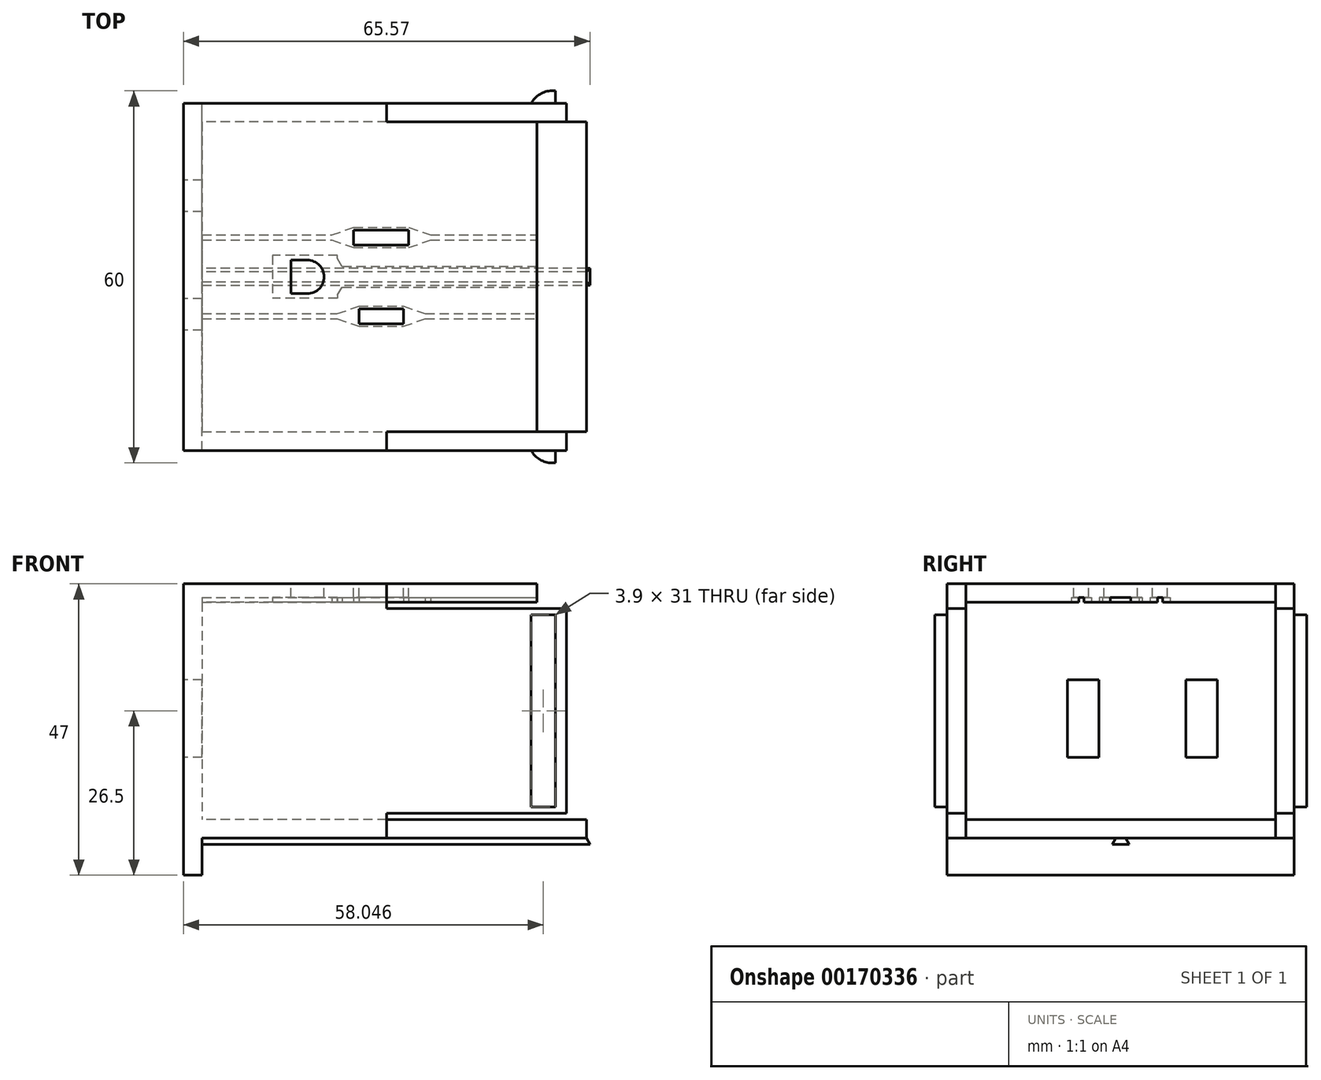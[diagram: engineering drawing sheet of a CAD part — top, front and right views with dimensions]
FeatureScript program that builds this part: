
annotation { "Feature Type Name" : "Feature", "Feature Type Description" : "" }
export const myFeature = defineFeature(function(context is Context, id is Id, definition is map)
    precondition{}
    {
        {
            var Q0;
            Q0=qCreatedBy(makeId("Top.planeOp"),FACE);
            var sketch = newSketch(context, id + "F0", { "sketchPlane" : qUnion([Q0])});
            skLineSegment(sketch, "E0", {"start": v(-33.77, 22.66) * mm, "end": v(-33.77, -33.34) * mm});
            skLineSegment(sketch, "E1", {"start": v(-33.77, -33.34) * mm, "end": v(31.23, -33.34) * mm});
            skLineSegment(sketch, "E2", {"start": v(31.23, -33.34) * mm, "end": v(31.23, 22.66) * mm});
            skLineSegment(sketch, "E3", {"start": v(31.23, 22.66) * mm, "end": v(-33.77, 22.66) * mm});
            skSolve(sketch);
        }
        {
            var Q0;
            Q0=makeQuery(id+"F0.imprint","IMPRINT",FACE,{"disambiguationData":[TD([[makeQuery(id+"F0.imprint","IMPRINT",EDGE,{"derivedFrom":sQuery(id+"F0.wireOp",EDGE,"E0")}),1.0]])]});
            extrude(context, id + "F1", {"entities" : qUnion([Q0]), "depth" : 41 * mm});
        }
        {
            var Q0;
            Q0=makeQuery(id+"F1.opExtrude","SWEPT_FACE",FACE,{"disambiguationData":[OSD([sQuery(id+"F0.wireOp",EDGE,"E2")])]});
            shell(context, id + "F2", {"entities" : qUnion([Q0]), "thickness" : 3 * mm});
        }
        {
            var Q0;
            Q0=makeQuery(id+"F1.opExtrude","SWEPT_FACE",FACE,{"disambiguationData":[OSD([sQuery(id+"F0.wireOp",EDGE,"E0")])]});
            var sketch = newSketch(context, id + "F3", { "sketchPlane" : qUnion([Q0])});
            skLineSegment(sketch, "E4.bottom", {"start": v(-10.28, 25.5) * mm, "end": v(-5.16, 25.5) * mm});
            skLineSegment(sketch, "E4.top", {"start": v(-10.28, 13) * mm, "end": v(-5.16, 13) * mm});
            skLineSegment(sketch, "E4.left", {"start": v(-10.28, 25.5) * mm, "end": v(-10.28, 13) * mm});
            skLineSegment(sketch, "E4.right", {"start": v(-5.16, 25.5) * mm, "end": v(-5.16, 13) * mm});
            skLineSegment(sketch, "E5.bottom", {"start": v(8.84, 25.5) * mm, "end": v(13.96, 25.5) * mm});
            skLineSegment(sketch, "E5.top", {"start": v(8.84, 13) * mm, "end": v(13.96, 13) * mm});
            skLineSegment(sketch, "E5.left", {"start": v(8.84, 25.5) * mm, "end": v(8.84, 13) * mm});
            skLineSegment(sketch, "E5.right", {"start": v(13.96, 25.5) * mm, "end": v(13.96, 13) * mm});
            skSolve(sketch);
        }
        {
            var Q0;
            Q0=makeQuery(id+"F3.imprint","IMPRINT",FACE,{"disambiguationData":[TD([[makeQuery(id+"F3.imprint","IMPRINT",EDGE,{"derivedFrom":sQuery(id+"F3.wireOp",EDGE,"E4.bottom")}),-1.0]])]});
            var Q1;
            Q1=makeQuery(id+"F3.imprint","IMPRINT",FACE,{"disambiguationData":[TD([[makeQuery(id+"F3.imprint","IMPRINT",EDGE,{"derivedFrom":sQuery(id+"F3.wireOp",EDGE,"E5.bottom")}),-1.0]])]});
            extrude(context, id + "F4", {"entities" : qUnion([Q0, Q1]), "operationType" : NewBodyOperationType.REMOVE, "oppositeDirection" : true, "depth" : 4.32 * mm});
        }
        {
            var Q0;
            Q0=makeQuery(id+"F1.opExtrude","SWEPT_FACE",FACE,{"disambiguationData":[OSD([sQuery(id+"F0.wireOp",EDGE,"E3")])]});
            var sketch = newSketch(context, id + "F5", { "sketchPlane" : qUnion([Q0])});
            skLineSegment(sketch, "E6.bottom", {"start": v(-22.33, 36) * mm, "end": v(-26.23, 36) * mm});
            skLineSegment(sketch, "E6.top", {"start": v(-22.33, 5) * mm, "end": v(-26.23, 5) * mm});
            skLineSegment(sketch, "E6.left", {"start": v(-22.33, 36) * mm, "end": v(-22.33, 5) * mm});
            skLineSegment(sketch, "E6.right", {"start": v(-26.23, 36) * mm, "end": v(-26.23, 5) * mm});
            skSolve(sketch);
        }
        {
            var Q0;
            Q0=makeQuery(id+"F5.imprint","IMPRINT",FACE,{"disambiguationData":[TD([[makeQuery(id+"F5.imprint","IMPRINT",EDGE,{"derivedFrom":sQuery(id+"F5.wireOp",EDGE,"E6.bottom")}),1.0]])]});
            extrude(context, id + "F6", {"entities" : qUnion([Q0]), "operationType" : NewBodyOperationType.ADD, "depth" : 2 * mm});
        }
        {
            var Q0;
            Q0=makeQuery(id+"F1.opExtrude","SWEPT_FACE",FACE,{"disambiguationData":[OSD([sQuery(id+"F0.wireOp",EDGE,"E1")])]});
            var sketch = newSketch(context, id + "F7", { "sketchPlane" : qUnion([Q0])});
            skLineSegment(sketch, "E7.bottom", {"start": v(26.23, 36) * mm, "end": v(22.33, 36) * mm});
            skLineSegment(sketch, "E7.top", {"start": v(26.23, 5) * mm, "end": v(22.33, 5) * mm});
            skLineSegment(sketch, "E7.left", {"start": v(26.23, 36) * mm, "end": v(26.23, 5) * mm});
            skLineSegment(sketch, "E7.right", {"start": v(22.33, 36) * mm, "end": v(22.33, 5) * mm});
            skSolve(sketch);
        }
        {
            var Q0;
            Q0=makeQuery(id+"F7.imprint","IMPRINT",FACE,{"disambiguationData":[TD([[makeQuery(id+"F7.imprint","IMPRINT",EDGE,{"derivedFrom":sQuery(id+"F7.wireOp",EDGE,"E7.bottom")}),1.0]])]});
            extrude(context, id + "F8", {"entities" : qUnion([Q0]), "operationType" : NewBodyOperationType.ADD, "depth" : 2 * mm});
        }
        {
            var Q0;
            Q0=makeQuery(id+"F6.opExtrude","CAP_EDGE",EDGE,{"disambiguationData":[OSD([sQuery(id+"F5.wireOp",EDGE,"E6.left")])],"isStart":false});
            var Q1;
            Q1=makeQuery(id+"F8.opExtrude","CAP_EDGE",EDGE,{"disambiguationData":[OSD([sQuery(id+"F7.wireOp",EDGE,"E7.right")])],"isStart":false});
            fillet(context, id + "F9", {"entities" : qUnion([Q0, Q1]), "radius" : 3.8 * mm, "tangentPropagation" : true, "allowEdgeOverflow" : false});
        }
        {
            var Q0;
            Q0=makeQuery(id+"F1.opExtrude","SWEPT_FACE",FACE,{"disambiguationData":[OSD([sQuery(id+"F0.wireOp",EDGE,"E3")])]});
            var sketch = newSketch(context, id + "F10", { "sketchPlane" : qUnion([Q0])});
            skLineSegment(sketch, "E8", {"start": v(-31.23, 38) * mm, "end": v(0.98, 38) * mm});
            skLineSegment(sketch, "E9", {"start": v(0.98, 38) * mm, "end": v(0.98, 37) * mm});
            skLineSegment(sketch, "E10", {"start": v(0.98, 37) * mm, "end": v(-28.02, 37) * mm});
            skLineSegment(sketch, "E11", {"start": v(-28.02, 37) * mm, "end": v(-28.02, 4) * mm});
            skLineSegment(sketch, "E12", {"start": v(-28.02, 4) * mm, "end": v(0.98, 4) * mm});
            skLineSegment(sketch, "E13", {"start": v(0.98, 4) * mm, "end": v(0.98, 3) * mm});
            skLineSegment(sketch, "E14", {"start": v(0.98, 3) * mm, "end": v(-31.23, 3) * mm});
            skLineSegment(sketch, "E15", {"start": v(-31.23, 3) * mm, "end": v(-31.23, 38) * mm});
            skSolve(sketch);
        }
        {
            var Q0;
            Q0=makeQuery(id+"F10.imprint","IMPRINT",FACE,{"disambiguationData":[TD([[makeQuery(id+"F10.imprint","IMPRINT",EDGE,{"derivedFrom":sQuery(id+"F10.wireOp",EDGE,"E8")}),-1.0]])]});
            extrude(context, id + "F11", {"entities" : qUnion([Q0]), "operationType" : NewBodyOperationType.REMOVE, "oppositeDirection" : true, "depth" : 66.3 * mm});
        }
        {
            var Q0;
            Q0=makeQuery(id+"F1.opExtrude","CAP_FACE",FACE,{"disambiguationData":[OSD([sQuery(id+"F0.wireOp",EDGE,"E0"),sQuery(id+"F0.wireOp",EDGE,"E1"),sQuery(id+"F0.wireOp",EDGE,"E2"),sQuery(id+"F0.wireOp",EDGE,"E3")])],"isStart":false});
            var sketch = newSketch(context, id + "F12", { "sketchPlane" : qUnion([Q0])});
            skLineSegment(sketch, "E16.bottom", {"start": v(31.23, -30.34) * mm, "end": v(23.23, -30.34) * mm});
            skLineSegment(sketch, "E16.top", {"start": v(31.23, 19.66) * mm, "end": v(23.23, 19.66) * mm});
            skLineSegment(sketch, "E16.left", {"start": v(31.23, -30.34) * mm, "end": v(31.23, 19.66) * mm});
            skLineSegment(sketch, "E16.right", {"start": v(23.23, -30.34) * mm, "end": v(23.23, 19.66) * mm});
            skSolve(sketch);
        }
        {
            var Q0;
            Q0=makeQuery(id+"F12.imprint","IMPRINT",FACE,{"disambiguationData":[TD([[makeQuery(id+"F12.imprint","IMPRINT",EDGE,{"derivedFrom":sQuery(id+"F12.wireOp",EDGE,"E16.bottom")}),-1.0]])]});
            extrude(context, id + "F13", {"entities" : qUnion([Q0]), "operationType" : NewBodyOperationType.REMOVE, "oppositeDirection" : true, "depth" : 14.73 * mm});
        }
        {
            var Q0;
            Q0=makeQuery(id+"F1.opExtrude","CAP_FACE",FACE,{"disambiguationData":[OSD([sQuery(id+"F0.wireOp",EDGE,"E0"),sQuery(id+"F0.wireOp",EDGE,"E1"),sQuery(id+"F0.wireOp",EDGE,"E2"),sQuery(id+"F0.wireOp",EDGE,"E3")])],"isStart":false});
            var sketch = newSketch(context, id + "F14", { "sketchPlane" : qUnion([Q0])});
            skLineSegment(sketch, "E17.bottom", {"start": v(2.57, 2.22) * mm, "end": v(-6.32, 2.22) * mm});
            skLineSegment(sketch, "E17.top", {"start": v(2.57, -0.2) * mm, "end": v(-6.32, -0.2) * mm});
            skLineSegment(sketch, "E17.left", {"start": v(2.57, 2.22) * mm, "end": v(2.57, -0.2) * mm});
            skLineSegment(sketch, "E17.right", {"start": v(-6.32, 2.22) * mm, "end": v(-6.32, -0.2) * mm});
            skCircle(sketch, "E18", {"center": v(-13.77, -5.34) * mm, "radius": 2.69 * mm});
            skLineSegment(sketch, "E19", {"start": v(-13.77, -2.65) * mm, "end": v(-16.46, -2.65) * mm});
            skLineSegment(sketch, "E20", {"start": v(-16.46, -2.65) * mm, "end": v(-16.46, -8.03) * mm});
            skLineSegment(sketch, "E21", {"start": v(-16.46, -8.03) * mm, "end": v(-13.77, -8.03) * mm});
            skLineSegment(sketch, "E22.bottom", {"start": v(1.73, -10.48) * mm, "end": v(-5.47, -10.48) * mm});
            skLineSegment(sketch, "E22.top", {"start": v(1.73, -12.9) * mm, "end": v(-5.47, -12.9) * mm});
            skLineSegment(sketch, "E22.left", {"start": v(1.73, -10.48) * mm, "end": v(1.73, -12.9) * mm});
            skLineSegment(sketch, "E22.right", {"start": v(-5.47, -10.48) * mm, "end": v(-5.47, -12.9) * mm});
            skSolve(sketch);
        }
        {
            var Q0;
            Q0=makeQuery(id+"F14.imprint","IMPRINT",FACE,{"disambiguationData":[TD([[makeQuery(id+"F14.imprint","IMPRINT",EDGE,{"derivedFrom":sQuery(id+"F14.wireOp",EDGE,"E17.bottom")}),1.0]])]});
            var Q1;
            {var subQ0=sQuery(id+"F14.wireOp",EDGE,"E18");var subQ1=makeQuery(id+"F14.imprint","INTERSECT",VERTEX,{"derivedFrom":[subQ0,sQuery(id+"F14.wireOp",EDGE,"E21")]});Q1=makeQuery(id+"F14.imprint","IMPRINT",FACE,{"disambiguationData":[TD([[makeQuery(id+"F14.imprint","IMPRINT",EDGE,{"disambiguationData":[TD([[subQ1,1.0]])],"derivedFrom":subQ0}),1.0]])]});}
            var Q2;
            Q2=makeQuery(id+"F14.imprint","IMPRINT",FACE,{"disambiguationData":[TD([[makeQuery(id+"F14.imprint","IMPRINT",EDGE,{"derivedFrom":sQuery(id+"F14.wireOp",EDGE,"E22.bottom")}),1.0]])]});
            var Q3;
            {var subQ0=sQuery(id+"F14.wireOp",EDGE,"E19");Q3=makeQuery(id+"F14.imprint","IMPRINT",FACE,{"disambiguationData":[TD([[makeQuery(id+"F14.imprint","IMPRINT",EDGE,{"derivedFrom":subQ0}),1.0]])]});}
            var Q4;
            {var subQ0=sQuery(id+"F14.wireOp",EDGE,"E21");Q4=makeQuery(id+"F14.imprint","IMPRINT",FACE,{"disambiguationData":[TD([[makeQuery(id+"F14.imprint","IMPRINT",EDGE,{"derivedFrom":subQ0}),1.0]])]});}
            extrude(context, id + "F15", {"entities" : qUnion([Q0, Q1, Q2, Q3, Q4]), "operationType" : NewBodyOperationType.REMOVE, "oppositeDirection" : true, "depth" : 25 * mm});
        }
        {
            var Q0;
            {var subQ0=sQuery(id+"F0.wireOp",EDGE,"E3");var subQ1=sQuery(id+"F0.wireOp",EDGE,"E2");var subQ2=sQuery(id+"F0.wireOp",EDGE,"E1");var subQ3=sQuery(id+"F0.wireOp",EDGE,"E0");Q0=makeQuery(id+"F11.boolean.opBoolean","MERGE",FACE,{"derivedFrom":[makeQuery(id+"F2.opShell","OFFSET_FACE",FACE,{"disambiguationData":[OSD([subQ3,subQ2,subQ1,subQ0]),TDD([makeQuery(id+"F1.opExtrude","CAP_FACE",FACE,{"disambiguationData":[OSD([subQ3,subQ2,subQ1,subQ0])],"isStart":false})])]}),makeQuery(id+"F11.opExtrude","SWEPT_FACE",FACE,{"disambiguationData":[OSD([sQuery(id+"F10.wireOp",EDGE,"E8")])]})]});}
            var sketch = newSketch(context, id + "F16", { "sketchPlane" : qUnion([Q0])});
            skLineSegment(sketch, "E23.bottom", {"start": v(-30.77, 11.29) * mm, "end": v(-30.77, 12.09) * mm});
            skLineSegment(sketch, "E23.top", {"start": v(23.23, 11.29) * mm, "end": v(23.23, 12.09) * mm});
            skLineSegment(sketch, "E24", {"start": v(-8.99, 11.29) * mm, "end": v(-5.47, 10.06) * mm});
            skLineSegment(sketch, "E25", {"start": v(-5.47, 10.06) * mm, "end": v(1.73, 10.06) * mm});
            skLineSegment(sketch, "E26", {"start": v(1.73, 10.06) * mm, "end": v(5.24, 11.29) * mm});
            skLineSegment(sketch, "E27", {"start": v(-8.99, 12.09) * mm, "end": v(-5.47, 13.32) * mm});
            skLineSegment(sketch, "E28", {"start": v(-5.47, 13.32) * mm, "end": v(1.73, 13.32) * mm});
            skLineSegment(sketch, "E29", {"start": v(1.73, 13.32) * mm, "end": v(5.24, 12.09) * mm});
            skLineSegment(sketch, "E30", {"start": v(-30.77, 11.29) * mm, "end": v(-8.99, 11.29) * mm});
            skLineSegment(sketch, "E31", {"start": v(5.24, 11.29) * mm, "end": v(23.23, 11.29) * mm});
            skLineSegment(sketch, "E32", {"start": v(-30.77, 12.09) * mm, "end": v(-8.99, 12.09) * mm});
            skLineSegment(sketch, "E33", {"start": v(5.24, 12.09) * mm, "end": v(23.23, 12.09) * mm});
            skSolve(sketch);
        }
        {
            var Q0;
            Q0=makeQuery(id+"F16.imprint","IMPRINT",FACE,{"disambiguationData":[TD([[makeQuery(id+"F16.imprint","IMPRINT",EDGE,{"derivedFrom":sQuery(id+"F16.wireOp",EDGE,"E23.bottom")}),-1.0]])]});
            extrude(context, id + "F17", {"entities" : qUnion([Q0]), "operationType" : NewBodyOperationType.REMOVE, "oppositeDirection" : true, "depth" : 0.8 * mm});
        }
        {
            var Q0;
            {var subQ2=sQuery(id+"F10.wireOp",EDGE,"E8");var subQ3=makeQuery(id+"F11.opExtrude","SWEPT_FACE",FACE,{"disambiguationData":[OSD([subQ2])]});var subQ4=sQuery(id+"F0.wireOp",EDGE,"E3");var subQ5=sQuery(id+"F0.wireOp",EDGE,"E2");var subQ6=sQuery(id+"F0.wireOp",EDGE,"E1");var subQ7=sQuery(id+"F0.wireOp",EDGE,"E0");var subQ8=makeQuery(id+"F2.opShell","OFFSET_FACE",FACE,{"disambiguationData":[OSD([subQ7,subQ6,subQ5,subQ4]),TDD([makeQuery(id+"F1.opExtrude","CAP_FACE",FACE,{"disambiguationData":[OSD([subQ7,subQ6,subQ5,subQ4])],"isStart":false})])]});var subQ9=makeQuery(id+"F11.boolean.opBoolean","MERGE",FACE,{"derivedFrom":[subQ8,subQ3]});var subQ12=makeQuery(id+"F1.opExtrude","SWEPT_FACE",FACE,{"disambiguationData":[OSD([subQ6])]});Q0=makeQuery(id+"F17.boolean.opBoolean","SPLIT",FACE,{"disambiguationData":[TD([subQ12])],"derivedFrom":subQ9});}
            var sketch = newSketch(context, id + "F18", { "sketchPlane" : qUnion([Q0])});
            skLineSegment(sketch, "E34.bottom", {"start": v(-0.98, -22.66) * mm, "end": v(31.23, -22.66) * mm});
            skLineSegment(sketch, "E34.top", {"start": v(-0.98, -19.66) * mm, "end": v(31.23, -19.66) * mm});
            skLineSegment(sketch, "E34.left", {"start": v(-0.98, -22.66) * mm, "end": v(-0.98, -19.66) * mm});
            skLineSegment(sketch, "E34.right", {"start": v(31.23, -22.66) * mm, "end": v(31.23, -19.66) * mm});
            skLineSegment(sketch, "E35.bottom", {"start": v(-0.98, 30.34) * mm, "end": v(31.23, 30.34) * mm});
            skLineSegment(sketch, "E35.top", {"start": v(-0.98, 33.34) * mm, "end": v(31.23, 33.34) * mm});
            skLineSegment(sketch, "E35.left", {"start": v(-0.98, 30.34) * mm, "end": v(-0.98, 33.34) * mm});
            skLineSegment(sketch, "E35.right", {"start": v(31.23, 30.34) * mm, "end": v(31.23, 33.34) * mm});
            skSolve(sketch);
        }
        {
            var Q0;
            Q0=makeQuery(id+"F18.imprint","IMPRINT",FACE,{"disambiguationData":[TD([[makeQuery(id+"F18.imprint","IMPRINT",EDGE,{"derivedFrom":sQuery(id+"F18.wireOp",EDGE,"E34.bottom")}),1.0]])]});
            var Q1;
            Q1=makeQuery(id+"F18.imprint","IMPRINT",FACE,{"disambiguationData":[TD([[makeQuery(id+"F18.imprint","IMPRINT",EDGE,{"derivedFrom":sQuery(id+"F18.wireOp",EDGE,"E35.top")}),1.0]])]});
            extrude(context, id + "F19", {"entities" : qUnion([Q0, Q1]), "operationType" : NewBodyOperationType.REMOVE, "oppositeDirection" : true, "depth" : 25 * mm});
        }
        {
            var Q0;
            Q0=makeQuery(id+"F1.opExtrude","CAP_FACE",FACE,{"disambiguationData":[OSD([sQuery(id+"F0.wireOp",EDGE,"E0"),sQuery(id+"F0.wireOp",EDGE,"E1"),sQuery(id+"F0.wireOp",EDGE,"E2"),sQuery(id+"F0.wireOp",EDGE,"E3")])],"isStart":true});
            var sketch = newSketch(context, id + "F20", { "sketchPlane" : qUnion([Q0])});
            skLineSegment(sketch, "E36.bottom", {"start": v(31.23, 33.34) * mm, "end": v(-0.98, 33.34) * mm});
            skLineSegment(sketch, "E36.top", {"start": v(31.23, 30.34) * mm, "end": v(-0.98, 30.34) * mm});
            skLineSegment(sketch, "E36.left", {"start": v(31.23, 33.34) * mm, "end": v(31.23, 30.34) * mm});
            skLineSegment(sketch, "E36.right", {"start": v(-0.98, 33.34) * mm, "end": v(-0.98, 30.34) * mm});
            skLineSegment(sketch, "E37.bottom", {"start": v(31.23, -22.66) * mm, "end": v(-0.98, -22.66) * mm});
            skLineSegment(sketch, "E37.top", {"start": v(31.23, -19.66) * mm, "end": v(-0.98, -19.66) * mm});
            skLineSegment(sketch, "E37.left", {"start": v(31.23, -22.66) * mm, "end": v(31.23, -19.66) * mm});
            skLineSegment(sketch, "E37.right", {"start": v(-0.98, -22.66) * mm, "end": v(-0.98, -19.66) * mm});
            skSolve(sketch);
        }
        {
            var Q0;
            Q0=makeQuery(id+"F20.imprint","IMPRINT",FACE,{"disambiguationData":[TD([[makeQuery(id+"F20.imprint","IMPRINT",EDGE,{"derivedFrom":sQuery(id+"F20.wireOp",EDGE,"E37.bottom")}),-1.0]])]});
            var Q1;
            Q1=makeQuery(id+"F20.imprint","IMPRINT",FACE,{"disambiguationData":[TD([[makeQuery(id+"F20.imprint","IMPRINT",EDGE,{"derivedFrom":sQuery(id+"F20.wireOp",EDGE,"E36.bottom")}),-1.0]])]});
            extrude(context, id + "F21", {"entities" : qUnion([Q0, Q1]), "operationType" : NewBodyOperationType.REMOVE, "oppositeDirection" : true, "depth" : 3.5 * mm});
        }
        {
            var Q0;
            Q0=makeQuery(id+"F1.opExtrude","CAP_FACE",FACE,{"disambiguationData":[OSD([sQuery(id+"F0.wireOp",EDGE,"E0"),sQuery(id+"F0.wireOp",EDGE,"E1"),sQuery(id+"F0.wireOp",EDGE,"E2"),sQuery(id+"F0.wireOp",EDGE,"E3")])],"isStart":true});
            var sketch = newSketch(context, id + "F22", { "sketchPlane" : qUnion([Q0])});
            skLineSegment(sketch, "E38.bottom", {"start": v(-33.77, 6.14) * mm, "end": v(31.23, 6.14) * mm});
            skLineSegment(sketch, "E38.top", {"start": v(-33.77, 4.54) * mm, "end": v(31.23, 4.54) * mm});
            skLineSegment(sketch, "E38.left", {"start": v(-33.77, 6.14) * mm, "end": v(-33.77, 4.54) * mm});
            skLineSegment(sketch, "E38.right", {"start": v(31.23, 6.14) * mm, "end": v(31.23, 4.54) * mm});
            skSolve(sketch);
        }
        {
            var Q0;
            Q0=makeQuery(id+"F22.imprint","IMPRINT",FACE,{"disambiguationData":[TD([[makeQuery(id+"F22.imprint","IMPRINT",EDGE,{"derivedFrom":sQuery(id+"F22.wireOp",EDGE,"E38.bottom")}),-1.0]])]});
            extrude(context, id + "F23", {"entities" : qUnion([Q0]), "operationType" : NewBodyOperationType.ADD, "depth" : 1 * mm, "hasDraft" : true, "draftAngle" : 30 * degree});
        }
        {
            var Q0;
            {var subQ0=sQuery(id+"F0.wireOp",EDGE,"E0");var subQ1=makeQuery(id+"F11.opExtrude","SWEPT_FACE",FACE,{"disambiguationData":[OSD([sQuery(id+"F10.wireOp",EDGE,"E8")])]});var subQ2=sQuery(id+"F0.wireOp",EDGE,"E3");var subQ4=sQuery(id+"F0.wireOp",EDGE,"E2");var subQ5=sQuery(id+"F0.wireOp",EDGE,"E1");var subQ6=makeQuery(id+"F2.opShell","OFFSET_FACE",FACE,{"disambiguationData":[OSD([subQ0,subQ5,subQ4,subQ2]),TDD([makeQuery(id+"F1.opExtrude","CAP_FACE",FACE,{"disambiguationData":[OSD([subQ0,subQ5,subQ4,subQ2])],"isStart":false})])]});var subQ7=makeQuery(id+"F1.opExtrude","SWEPT_FACE",FACE,{"disambiguationData":[OSD([subQ2])]});Q0=makeQuery(id+"F17.boolean.opBoolean","SPLIT",FACE,{"disambiguationData":[TD([subQ7])],"derivedFrom":makeQuery(id+"F11.boolean.opBoolean","MERGE",FACE,{"derivedFrom":[subQ6,subQ1]})});}
            var sketch = newSketch(context, id + "F24", { "sketchPlane" : qUnion([Q0])});
            skLineSegment(sketch, "E39", {"start": v(23.23, 6.99) * mm, "end": v(23.23, 3.69) * mm});
            skLineSegment(sketch, "E40", {"start": v(23.23, 3.69) * mm, "end": v(-8.17, 3.69) * mm});
            skLineSegment(sketch, "E41", {"start": v(-8.17, 3.69) * mm, "end": v(-8.92, 2.39) * mm});
            skLineSegment(sketch, "E42", {"start": v(-8.92, 8.29) * mm, "end": v(-8.17, 6.99) * mm});
            skLineSegment(sketch, "E43", {"start": v(-8.17, 6.99) * mm, "end": v(23.23, 6.99) * mm});
            skLineSegment(sketch, "E44", {"start": v(-8.92, 2.39) * mm, "end": v(-8.92, 1.89) * mm});
            skLineSegment(sketch, "E45", {"start": v(-8.92, 1.89) * mm, "end": v(-19.43, 1.89) * mm});
            skLineSegment(sketch, "E46", {"start": v(-8.92, 8.29) * mm, "end": v(-8.92, 8.79) * mm});
            skLineSegment(sketch, "E47", {"start": v(-8.92, 8.79) * mm, "end": v(-19.43, 8.79) * mm});
            skLineSegment(sketch, "E48", {"start": v(-19.43, 1.89) * mm, "end": v(-19.43, 8.79) * mm});
            skSolve(sketch);
        }
        {
            var Q0;
            Q0=makeQuery(id+"F24.imprint","IMPRINT",FACE,{"disambiguationData":[TD([[makeQuery(id+"F24.imprint","IMPRINT",EDGE,{"derivedFrom":sQuery(id+"F24.wireOp",EDGE,"E39")}),-1.0]])]});
            extrude(context, id + "F25", {"entities" : qUnion([Q0]), "operationType" : NewBodyOperationType.REMOVE, "oppositeDirection" : true, "depth" : 0.8 * mm});
        }
        {
            var Q0;
            {var subQ0=sQuery(id+"F0.wireOp",EDGE,"E0");var subQ1=makeQuery(id+"F11.opExtrude","SWEPT_FACE",FACE,{"disambiguationData":[OSD([sQuery(id+"F10.wireOp",EDGE,"E8")])]});var subQ2=sQuery(id+"F0.wireOp",EDGE,"E3");var subQ4=sQuery(id+"F0.wireOp",EDGE,"E2");var subQ5=sQuery(id+"F0.wireOp",EDGE,"E1");var subQ6=makeQuery(id+"F2.opShell","OFFSET_FACE",FACE,{"disambiguationData":[OSD([subQ0,subQ5,subQ4,subQ2]),TDD([makeQuery(id+"F1.opExtrude","CAP_FACE",FACE,{"disambiguationData":[OSD([subQ0,subQ5,subQ4,subQ2])],"isStart":false})])]});var subQ7=makeQuery(id+"F1.opExtrude","SWEPT_FACE",FACE,{"disambiguationData":[OSD([subQ2])]});Q0=makeQuery(id+"F17.boolean.opBoolean","SPLIT",FACE,{"disambiguationData":[TD([subQ7])],"derivedFrom":makeQuery(id+"F11.boolean.opBoolean","MERGE",FACE,{"derivedFrom":[subQ6,subQ1]})});}
            var sketch = newSketch(context, id + "F26", { "sketchPlane" : qUnion([Q0])});
            skLineSegment(sketch, "E49.bottom", {"start": v(-30.77, -1.41) * mm, "end": v(-30.77, -0.61) * mm});
            skLineSegment(sketch, "E49.top", {"start": v(23.23, -1.41) * mm, "end": v(23.23, -0.61) * mm});
            skLineSegment(sketch, "E50", {"start": v(-9.83, -1.41) * mm, "end": v(-6.32, -2.64) * mm});
            skLineSegment(sketch, "E51", {"start": v(-6.32, -2.64) * mm, "end": v(2.57, -2.64) * mm});
            skLineSegment(sketch, "E52", {"start": v(2.57, -2.64) * mm, "end": v(6.08, -1.41) * mm});
            skLineSegment(sketch, "E53", {"start": v(-9.83, -0.61) * mm, "end": v(-6.32, 0.62) * mm});
            skLineSegment(sketch, "E54", {"start": v(-6.32, 0.62) * mm, "end": v(2.57, 0.62) * mm});
            skLineSegment(sketch, "E55", {"start": v(2.57, 0.62) * mm, "end": v(6.08, -0.61) * mm});
            skLineSegment(sketch, "E56", {"start": v(-30.77, -1.41) * mm, "end": v(-9.83, -1.41) * mm});
            skLineSegment(sketch, "E57", {"start": v(6.08, -1.41) * mm, "end": v(23.23, -1.41) * mm});
            skLineSegment(sketch, "E58", {"start": v(-30.77, -0.61) * mm, "end": v(-9.83, -0.61) * mm});
            skLineSegment(sketch, "E59", {"start": v(6.08, -0.61) * mm, "end": v(23.23, -0.61) * mm});
            skSolve(sketch);
        }
        {
            var Q0;
            Q0=makeQuery(id+"F26.imprint","IMPRINT",FACE,{"disambiguationData":[TD([[makeQuery(id+"F26.imprint","IMPRINT",EDGE,{"derivedFrom":sQuery(id+"F26.wireOp",EDGE,"E49.bottom")}),-1.0]])]});
            extrude(context, id + "F27", {"entities" : qUnion([Q0]), "operationType" : NewBodyOperationType.REMOVE, "oppositeDirection" : true, "depth" : 0.8 * mm});
        }
        {
            var Q0;
            Q0=makeQuery(id+"F23.opExtrude","CAP_FACE",FACE,{"disambiguationData":[OSD([sQuery(id+"F22.wireOp",EDGE,"E38.bottom"),sQuery(id+"F22.wireOp",EDGE,"E38.top"),sQuery(id+"F22.wireOp",EDGE,"E38.left"),sQuery(id+"F22.wireOp",EDGE,"E38.right")])],"isStart":false});
            var sketch = newSketch(context, id + "F28", { "sketchPlane" : qUnion([Q0])});
            skLineSegment(sketch, "E60.bottom", {"start": v(-34.35, 3.96) * mm, "end": v(-33.77, 3.96) * mm});
            skLineSegment(sketch, "E60.top", {"start": v(-34.35, 6.72) * mm, "end": v(-33.77, 6.72) * mm});
            skLineSegment(sketch, "E60.left", {"start": v(-34.35, 3.96) * mm, "end": v(-34.35, 6.72) * mm});
            skLineSegment(sketch, "E60.right", {"start": v(-33.77, 3.96) * mm, "end": v(-33.77, 6.72) * mm});
            skSolve(sketch);
        }
        {
            var Q0;
            Q0=makeQuery(id+"F28.imprint","IMPRINT",FACE,{"disambiguationData":[TD([[makeQuery(id+"F28.imprint","IMPRINT",EDGE,{"derivedFrom":sQuery(id+"F28.wireOp",EDGE,"E60.bottom")}),1.0]])]});
            extrude(context, id + "F29", {"entities" : qUnion([Q0]), "operationType" : NewBodyOperationType.REMOVE, "oppositeDirection" : true, "depth" : 25 * mm});
        }
        {
            var Q0;
            {var subQ0=sQuery(id+"F0.wireOp",EDGE,"E1");var subQ1=sQuery(id+"F0.wireOp",EDGE,"E3");var subQ2=sQuery(id+"F0.wireOp",EDGE,"E2");var subQ3=sQuery(id+"F0.wireOp",EDGE,"E0");var subQ4=makeQuery(id+"F1.opExtrude","CAP_FACE",FACE,{"disambiguationData":[OSD([subQ3,subQ0,subQ2,subQ1])],"isStart":true});var subQ5=makeQuery(id+"F1.opExtrude","SWEPT_FACE",FACE,{"disambiguationData":[OSD([subQ0])]});Q0=makeQuery(id+"F23.boolean.opBoolean","SPLIT",FACE,{"disambiguationData":[TD([subQ5])],"derivedFrom":subQ4});}
            var sketch = newSketch(context, id + "F30", { "sketchPlane" : qUnion([Q0])});
            skLineSegment(sketch, "E61.bottom", {"start": v(-33.77, 33.34) * mm, "end": v(-30.77, 33.34) * mm});
            skLineSegment(sketch, "E61.top", {"start": v(-33.77, -22.66) * mm, "end": v(-30.77, -22.66) * mm});
            skLineSegment(sketch, "E61.left", {"start": v(-33.77, 33.34) * mm, "end": v(-33.77, -22.66) * mm});
            skLineSegment(sketch, "E61.right", {"start": v(-30.77, 33.34) * mm, "end": v(-30.77, -22.66) * mm});
            skSolve(sketch);
        }
        {
            var Q0;
            {var subQ0=sQuery(id+"F30.wireOp",EDGE,"E61.bottom");Q0=makeQuery(id+"F30.imprint","IMPRINT",FACE,{"disambiguationData":[TD([[makeQuery(id+"F30.imprint","IMPRINT",EDGE,{"derivedFrom":subQ0}),-1.0]])]});}
            var Q1;
            {var subQ0=sQuery(id+"F30.wireOp",EDGE,"E61.top");Q1=makeQuery(id+"F30.imprint","IMPRINT",FACE,{"disambiguationData":[TD([[makeQuery(id+"F30.imprint","IMPRINT",EDGE,{"derivedFrom":subQ0}),1.0]])]});}
            extrude(context, id + "F31", {"entities" : qUnion([Q0, Q1]), "operationType" : NewBodyOperationType.ADD, "depth" : 6 * mm});
        }
    });
